# Revit family: Basic_Valves-Full_Port-WATTS-LFM1115_12in_Globe_300
name_source: partatom
category: Pipe Accessories
revit_build: Autodesk Revit 2016 (Build: 20150714_1515(x64)
units: mm (PartAtom-declared; Revit-internal decimal feet)

## family parameters
Always vertical = Yes
Cut with Voids When Loaded = No
OmniClass Number = 23.65.55.14
OmniClass Title = Valves for Liquid Services
Part Type = Valve - Normal
Round Connector Dimension = Use Radius
Shared = Yes
Work Plane-Based = No

## types (1)
- LFM115 - 12" (Globe 300#)
    Body Radius = 6 1/2"
    Center to Top = 20 7/8"
    Connection Radius = 6"
    Connection Size = 12"
    Connection Type = 300#
    Country = United States
    Description = The Watts ACV Models M100 are full port, single chamber basic valves that incorporate a one-piece disc and diaphragm assembly. This assembly is the only moving part within the valve allowing it to open, close, or modulate as commanded by the pilot control system.
    Flange Geometry = Yes
    Flange Radius = 7 1/2"
    Flange Thickness = 1 1/2"
    Inlet Connection = 12" Inlet Connection
    Inner Length = 16 1/4"
    Lenght 2 = 35 1/2"
    Manufacturer = WATTS
    Manufacturer Product Line = Automatic Control Valves
    Material = Metal-WATTS-Ductile Iron
    Model = M100
    NPT Port Size K = 1"
    NPT Port Size K radius = 1/8"
    Nominal Dist. = 1 13/32"
    Nominal Height = 6 31/32"
    Nominal Radius 1 = 3/8"
    Nominal Radius 2  ( L ) = 1 1/4"
    Nominal Thickness = 2"
    Nominal Width = 8 1/2"
    Outlet Connection = 12" Outlet Connection
    Overall Length = 35 1/2"
    Pressure Rating = 400.00 psi
    Price = Prices may vary. Please consult Manufacturer Representative for most up-to-date price list.
    Product Documentation Link = http://media.wattswater.com
    Product Page URL = https://www.watts.com
    Region = North America
    Top Port ( K ) Connection Location = 2 27/32"
    URL = http://www.watts.com
    Warranty Information = 1 Year (Limited)
    Weight = 1500 lbs. 680 kgs.

## geometry (parser evidence)
native form markers: Sweep x5
no freeform markers — native parametric forms only
